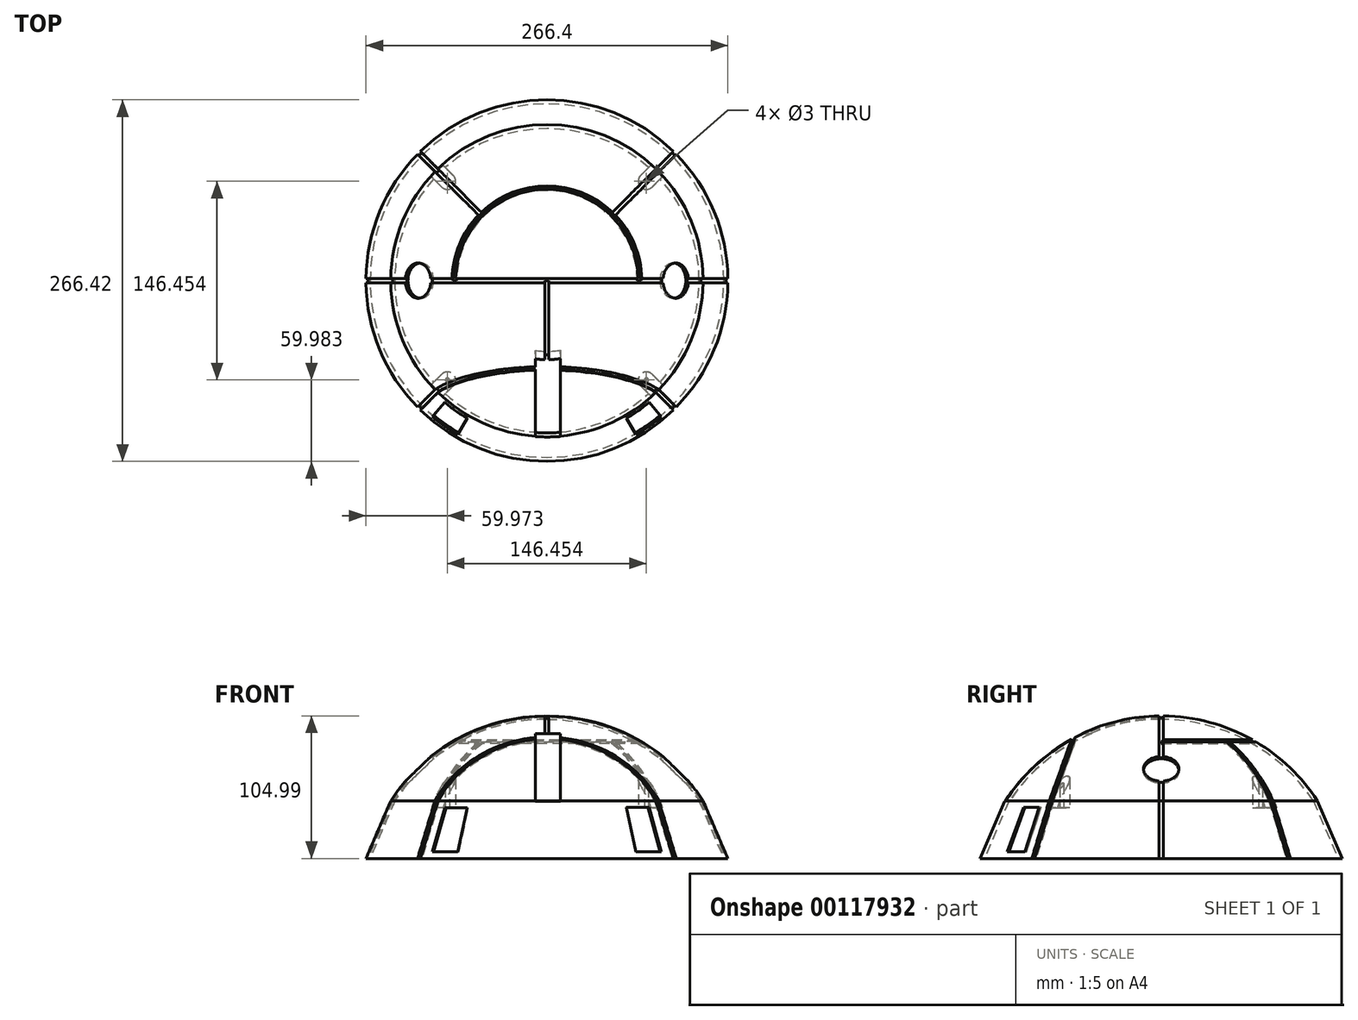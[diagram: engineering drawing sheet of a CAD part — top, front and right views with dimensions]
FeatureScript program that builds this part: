
annotation { "Feature Type Name" : "Feature", "Feature Type Description" : "" }
export const myFeature = defineFeature(function(context is Context, id is Id, definition is map)
    precondition{}
    {
        {
            var Q0;
            Q0=qCreatedBy(makeId("Front.planeOp"),FACE);
            var sketch = newSketch(context, id + "F0", { "sketchPlane" : qUnion([Q0])});
            skArc(sketch, "E0", {"start": v(114.97, 74.5) * mm, "mid": v(0, 137) * mm, "end": v(-114.97, 74.5) * mm});
            skLineSegment(sketch, "E1", {"start": v(-137, 0) * mm, "end": v(137, 0) * mm});
            skLineSegment(sketch, "E2", {"start": v(-133.21, 32) * mm, "end": v(133.21, 32) * mm});
            skLineSegment(sketch, "E3", {"start": v(-114.97, 74.5) * mm, "end": v(114.97, 74.5) * mm});
            skLineSegment(sketch, "E4", {"start": v(-114.97, 74.5) * mm, "end": v(-133.21, 32) * mm});
            skLineSegment(sketch, "E5", {"start": v(114.97, 74.5) * mm, "end": v(133.21, 32) * mm});
            skLineSegment(sketch, "E6", {"start": v(0, 137) * mm, "end": v(-99.44, 137) * mm, "construction": true});
            skLineSegment(sketch, "E7", {"start": v(0, 0) * mm, "end": v(0, 137) * mm});
            skArc(sketch, "E8", {"start": v(130.64, 32) * mm, "mid": v(0, 134.5) * mm, "end": v(-130.64, 32) * mm});
            skLineSegment(sketch, "E9", {"start": v(-111.98, 74.5) * mm, "end": v(-130.22, 32) * mm});
            skLineSegment(sketch, "E10", {"start": v(111.98, 74.5) * mm, "end": v(130.64, 32) * mm});
            skLineSegment(sketch, "E11", {"start": v(-111.98, 74.5) * mm, "end": v(-111.98, 32) * mm});
            skSolve(sketch);
        }
        {
            var Q0;
            {var subQ0=sQuery(id+"F0.wireOp",EDGE,"E4");Q0=makeQuery(id+"F0.imprint","IMPRINT",FACE,{"disambiguationData":[TD([[makeQuery(id+"F0.imprint","IMPRINT",EDGE,{"derivedFrom":subQ0}),1.0]])]});}
            var Q1;
            {var subQ0=sQuery(id+"F0.wireOp",EDGE,"E9");var subQ5=sQuery(id+"F0.wireOp",EDGE,"E2");var subQ7=makeQuery(id+"F0.imprint","INTERSECT",VERTEX,{"derivedFrom":[subQ5,subQ0]});Q1=makeQuery(id+"F0.imprint","IMPRINT",FACE,{"disambiguationData":[TD([[makeQuery(id+"F0.imprint","IMPRINT",EDGE,{"disambiguationData":[TD([[subQ7,1.0]])],"derivedFrom":subQ5}),1.0]])]});}
            var Q2;
            {var subQ0=sQuery(id+"F0.wireOp",EDGE,"y0KMc1JP-Vqzv-Jfck-pHGM-2HrRGkrfssAq");Q2=makeQuery(id+"F0.imprint","IMPRINT",FACE,{"disambiguationData":[TD([[makeQuery(id+"F0.imprint","IMPRINT",EDGE,{"derivedFrom":subQ0}),-1.0]])]});}
            var Q3;
            {var subQ1=sQuery(id+"F0.wireOp",EDGE,"E0");var subQ3=sQuery(id+"F0.wireOp",EDGE,"E7");var subQ4=makeQuery(id+"F0.imprint","INTERSECT",VERTEX,{"derivedFrom":[subQ1,subQ3]});Q3=makeQuery(id+"F0.imprint","IMPRINT",FACE,{"disambiguationData":[TD([[makeQuery(id+"F0.imprint","IMPRINT",EDGE,{"disambiguationData":[TD([[subQ4,1.0]])],"derivedFrom":subQ3}),1.0]])]});}
            var Q4;
            Q4=sQuery(id+"F0.wireOp",EDGE,"E7");
            revolve(context, id + "F1", {"entities" : qUnion([Q0, Q1, Q2, Q3]), "axis" : qUnion([Q4]), "revolveType" : RevolveType.FULL});
        }
        {
            var Q0;
            Q0=qCreatedBy(makeId("Top.planeOp"),FACE);
            cPlane(context, id + "F2", {"entities" : qUnion([Q0]), "cplaneType" : CPlaneType.OFFSET, "offset" : 74.5 * mm, "width" : 150 * mm, "height" : 150 * mm});
        }
        {
            var Q0;
            Q0=qCreatedBy(id+"F2.planeOp",FACE);
            var sketch = newSketch(context, id + "F3", { "sketchPlane" : qUnion([Q0])});
            skLineSegment(sketch, "E12", {"start": v(0, 0) * mm, "end": v(-58.68, 0) * mm, "construction": true});
            skLineSegment(sketch, "E13.bottom", {"start": v(-113.47, 1.5) * mm, "end": v(-116.47, 1.5) * mm});
            skLineSegment(sketch, "E13.top", {"start": v(-113.47, -1.5) * mm, "end": v(-116.47, -1.5) * mm});
            skLineSegment(sketch, "E13.left", {"start": v(-113.47, 1.5) * mm, "end": v(-113.47, -1.5) * mm});
            skLineSegment(sketch, "E13.right", {"start": v(-116.47, 1.5) * mm, "end": v(-116.47, -1.5) * mm});
            skPoint(sketch, "E13.middle", {"position": v(-114.97, 0) * mm});
            skLineSegment(sketch, "E14.1.0", {"start": v(-81.3, -79.18) * mm, "end": v(-83.42, -81.3) * mm});
            skLineSegment(sketch, "E14.1.1", {"start": v(-81.3, -79.18) * mm, "end": v(-79.18, -81.3) * mm});
            skLineSegment(sketch, "E14.1.2", {"start": v(-79.18, -81.3) * mm, "end": v(-81.3, -83.42) * mm});
            skLineSegment(sketch, "E14.1.3", {"start": v(-83.42, -81.3) * mm, "end": v(-81.3, -83.42) * mm});
            skLineSegment(sketch, "E14.2.0", {"start": v(-1.5, -113.47) * mm, "end": v(-1.5, -116.47) * mm});
            skLineSegment(sketch, "E14.2.1", {"start": v(-1.5, -113.47) * mm, "end": v(1.5, -113.47) * mm});
            skLineSegment(sketch, "E14.2.2", {"start": v(1.5, -113.47) * mm, "end": v(1.5, -116.47) * mm});
            skLineSegment(sketch, "E14.2.3", {"start": v(-1.5, -116.47) * mm, "end": v(1.5, -116.47) * mm});
            skLineSegment(sketch, "E14.3.0", {"start": v(79.18, -81.3) * mm, "end": v(81.3, -83.42) * mm});
            skLineSegment(sketch, "E14.3.1", {"start": v(79.18, -81.3) * mm, "end": v(81.3, -79.18) * mm});
            skLineSegment(sketch, "E14.3.2", {"start": v(81.3, -79.18) * mm, "end": v(83.42, -81.3) * mm});
            skLineSegment(sketch, "E14.3.3", {"start": v(81.3, -83.42) * mm, "end": v(83.42, -81.3) * mm});
            skLineSegment(sketch, "E14.4.0", {"start": v(113.47, -1.5) * mm, "end": v(116.47, -1.5) * mm});
            skLineSegment(sketch, "E14.4.1", {"start": v(113.47, -1.5) * mm, "end": v(113.47, 1.5) * mm});
            skLineSegment(sketch, "E14.4.2", {"start": v(113.47, 1.5) * mm, "end": v(116.47, 1.5) * mm});
            skLineSegment(sketch, "E14.4.3", {"start": v(116.47, -1.5) * mm, "end": v(116.47, 1.5) * mm});
            skLineSegment(sketch, "E14.5.0", {"start": v(81.3, 79.18) * mm, "end": v(83.42, 81.3) * mm});
            skLineSegment(sketch, "E14.5.1", {"start": v(81.3, 79.18) * mm, "end": v(79.18, 81.3) * mm});
            skLineSegment(sketch, "E14.5.2", {"start": v(79.18, 81.3) * mm, "end": v(81.3, 83.42) * mm});
            skLineSegment(sketch, "E14.5.3", {"start": v(83.42, 81.3) * mm, "end": v(81.3, 83.42) * mm});
            skLineSegment(sketch, "E14.6.0", {"start": v(1.5, 113.47) * mm, "end": v(1.5, 116.47) * mm});
            skLineSegment(sketch, "E14.6.1", {"start": v(1.5, 113.47) * mm, "end": v(-1.5, 113.47) * mm});
            skLineSegment(sketch, "E14.6.2", {"start": v(-1.5, 113.47) * mm, "end": v(-1.5, 116.47) * mm});
            skLineSegment(sketch, "E14.6.3", {"start": v(1.5, 116.47) * mm, "end": v(-1.5, 116.47) * mm});
            skLineSegment(sketch, "E14.7.0", {"start": v(-79.18, 81.3) * mm, "end": v(-81.3, 83.42) * mm});
            skLineSegment(sketch, "E14.7.1", {"start": v(-79.18, 81.3) * mm, "end": v(-81.3, 79.18) * mm});
            skLineSegment(sketch, "E14.7.2", {"start": v(-81.3, 79.18) * mm, "end": v(-83.42, 81.3) * mm});
            skLineSegment(sketch, "E14.7.3", {"start": v(-81.3, 83.42) * mm, "end": v(-83.42, 81.3) * mm});
            skPoint(sketch, "E14.center", {"position": v(0, 0) * mm});
            skLineSegment(sketch, "E15", {"start": v(81.3, -81.3) * mm, "end": v(-81.3, 81.3) * mm, "construction": true});
            skLineSegment(sketch, "E16", {"start": v(81.3, 81.3) * mm, "end": v(-81.3, -81.3) * mm, "construction": true});
            skLineSegment(sketch, "E17", {"start": v(-81.3, -81.3) * mm, "end": v(81.3, -81.3) * mm, "construction": true});
            skSolve(sketch);
        }
        {
            var Q0;
            Q0=makeQuery(id+"F3.imprint","IMPRINT",FACE,{"disambiguationData":[TD([[makeQuery(id+"F3.imprint","IMPRINT",EDGE,{"derivedFrom":sQuery(id+"F3.wireOp",EDGE,"E13.bottom")}),1.0]])]});
            var Q1;
            Q1=sQuery(id+"F0.wireOp",EDGE,"E4");
            sweep(context, id + "F4", {"operationType" : NewBodyOperationType.REMOVE, "profiles" : qUnion([Q0]), "path" : qUnion([Q1])});
        }
        {
            var Q0;
            Q0=makeQuery(id+"F3.imprint","IMPRINT",FACE,{"disambiguationData":[TD([[makeQuery(id+"F3.imprint","IMPRINT",EDGE,{"derivedFrom":sQuery(id+"F3.wireOp",EDGE,"E13.bottom")}),1.0]])]});
            var Q1;
            Q1=sQuery(id+"F0.wireOp",EDGE,"E0");
            sweep(context, id + "F5", {"operationType" : NewBodyOperationType.REMOVE, "profiles" : qUnion([Q0]), "path" : qUnion([Q1])});
        }
        {
            var Q0;
            Q0=makeQuery(id+"F3.imprint","IMPRINT",FACE,{"disambiguationData":[TD([[makeQuery(id+"F3.imprint","IMPRINT",EDGE,{"derivedFrom":sQuery(id+"F3.wireOp",EDGE,"E14.4.0")}),1.0]])]});
            var Q1;
            Q1=sQuery(id+"F0.wireOp",EDGE,"E5");
            sweep(context, id + "F6", {"operationType" : NewBodyOperationType.REMOVE, "profiles" : qUnion([Q0]), "path" : qUnion([Q1])});
        }
        {
            var Q0;
            Q0=qCreatedBy(makeId("Right.planeOp"),FACE);
            var sketch = newSketch(context, id + "F7", { "sketchPlane" : qUnion([Q0])});
            skArc(sketch, "E18", {"start": v(0, 137) * mm, "mid": v(-33.14, 132.93) * mm, "end": v(-64.32, 120.96) * mm});
            skLineSegment(sketch, "E19", {"start": v(0, 0) * mm, "end": v(-64.32, 120.96) * mm, "construction": true});
            skLineSegment(sketch, "E20", {"start": v(0, 137) * mm, "end": v(0, 0) * mm, "construction": true});
            skSolve(sketch);
        }
        {
            var Q0;
            Q0=qCreatedBy(makeId("Front.planeOp"),FACE);
            var sketch = newSketch(context, id + "F8", { "sketchPlane" : qUnion([Q0])});
            skLineSegment(sketch, "E21.bottom", {"start": v(1.5, 138.5) * mm, "end": v(-1.5, 138.5) * mm});
            skLineSegment(sketch, "E21.top", {"start": v(1.5, 135.5) * mm, "end": v(-1.5, 135.5) * mm});
            skLineSegment(sketch, "E21.left", {"start": v(1.5, 138.5) * mm, "end": v(1.5, 135.5) * mm});
            skLineSegment(sketch, "E21.right", {"start": v(-1.5, 138.5) * mm, "end": v(-1.5, 135.5) * mm});
            skPoint(sketch, "E21.middle", {"position": v(0, 137) * mm});
            skSolve(sketch);
        }
        {
            var Q0;
            Q0=makeQuery(id+"F8.imprint","IMPRINT",FACE,{"disambiguationData":[TD([[makeQuery(id+"F8.imprint","IMPRINT",EDGE,{"derivedFrom":sQuery(id+"F8.wireOp",EDGE,"E21.bottom")}),1.0]])]});
            var Q1;
            Q1=sQuery(id+"F7.wireOp",EDGE,"E18");
            sweep(context, id + "F9", {"operationType" : NewBodyOperationType.REMOVE, "profiles" : qUnion([Q0]), "path" : qUnion([Q1])});
        }
        {
            var Q0;
            Q0=qCreatedBy(makeId("Front.planeOp"),FACE);
            var sketch = newSketch(context, id + "F10", { "sketchPlane" : qUnion([Q0])});
            skCircle(sketch, "E22", {"center": v(0, 0) * mm, "radius": 137 * mm, "construction": true});
            skLineSegment(sketch, "E23", {"start": v(0, 0) * mm, "end": v(68.5, 118.65) * mm, "construction": true});
            skLineSegment(sketch, "E24", {"start": v(68.5, 118.65) * mm, "end": v(-68.5, 118.65) * mm});
            skLineSegment(sketch, "E25", {"start": v(-68.5, 118.65) * mm, "end": v(0, 0) * mm, "construction": true});
            skCircle(sketch, "E26", {"center": v(68.5, 118.65) * mm, "radius": 1.5 * mm});
            skLineSegment(sketch, "E27", {"start": v(67.75, 117.35) * mm, "end": v(69.05, 116.6) * mm});
            skLineSegment(sketch, "E28", {"start": v(69.05, 116.6) * mm, "end": v(70.55, 119.2) * mm});
            skLineSegment(sketch, "E29", {"start": v(67.75, 117.35) * mm, "end": v(66.45, 118.1) * mm});
            skLineSegment(sketch, "E30", {"start": v(70.55, 119.2) * mm, "end": v(67.95, 120.7) * mm});
            skLineSegment(sketch, "E31", {"start": v(67.95, 120.7) * mm, "end": v(66.45, 118.1) * mm});
            skLineSegment(sketch, "E32", {"start": v(0, 0) * mm, "end": v(104.95, 88.06) * mm, "construction": true});
            skLineSegment(sketch, "E33", {"start": v(0, 0) * mm, "end": v(-104.95, 88.06) * mm, "construction": true});
            skLineSegment(sketch, "E34", {"start": v(0, 0) * mm, "end": v(-114.71, 74.9) * mm, "construction": true});
            skLineSegment(sketch, "E35", {"start": v(-104.95, 88.06) * mm, "end": v(-81.98, 115.43) * mm});
            skLineSegment(sketch, "E36", {"start": v(104.95, 88.06) * mm, "end": v(89.01, 107.05) * mm});
            skSolve(sketch);
        }
        {
            var Q0;
            Q0=sQuery(id+"F10.wireOp",EDGE,"E24");
            cPlane(context, id + "F11", {"entities" : qUnion([Q0]), "cplaneType" : CPlaneType.LINE_ANGLE, "offset" : 25 * mm, "angle" : 90 * degree, "width" : 150 * mm, "height" : 150 * mm});
        }
        {
            var Q0;
            Q0=qCreatedBy(id+"F11.planeOp",FACE);
            var sketch = newSketch(context, id + "F12", { "sketchPlane" : qUnion([Q0])});
            skArc(sketch, "E37", {"start": v(68.5, 0) * mm, "mid": v(0, 68.5) * mm, "end": v(-68.5, 0) * mm});
            skLineSegment(sketch, "E38", {"start": v(-68.5, 0) * mm, "end": v(68.5, 0) * mm});
            skSolve(sketch);
        }
        {
            var Q0;
            {var subQ0=sQuery(id+"F10.wireOp",EDGE,"E26");var subQ3=makeQuery(id+"F10.imprint","INTERSECT",VERTEX,{"derivedFrom":[subQ0,sQuery(id+"F10.wireOp",EDGE,"E31")]});Q0=makeQuery(id+"F10.imprint","IMPRINT",FACE,{"disambiguationData":[TD([[makeQuery(id+"F10.imprint","IMPRINT",EDGE,{"disambiguationData":[TD([[subQ3,1.0]])],"derivedFrom":subQ0}),1.0]])]});}
            var Q1;
            {var subQ5=sQuery(id+"F10.wireOp",EDGE,"E29");Q1=makeQuery(id+"F10.imprint","IMPRINT",FACE,{"disambiguationData":[TD([[makeQuery(id+"F10.imprint","IMPRINT",EDGE,{"derivedFrom":subQ5}),-1.0]])]});}
            var Q2;
            {var subQ0=sQuery(id+"F10.wireOp",EDGE,"E31");var subQ1=sQuery(id+"F10.wireOp",EDGE,"E24");var subQ2=makeQuery(id+"F10.imprint","INTERSECT",VERTEX,{"derivedFrom":[subQ1,subQ0]});Q2=makeQuery(id+"F10.imprint","IMPRINT",FACE,{"disambiguationData":[TD([[makeQuery(id+"F10.imprint","IMPRINT",EDGE,{"disambiguationData":[TD([[subQ2,1.0]])],"derivedFrom":subQ1}),-1.0]])]});}
            var Q3;
            {var subQ0=sQuery(id+"F10.wireOp",EDGE,"E31");var subQ1=sQuery(id+"F10.wireOp",EDGE,"E26");var subQ2=makeQuery(id+"F10.imprint","INTERSECT",VERTEX,{"derivedFrom":[subQ1,subQ0]});Q3=makeQuery(id+"F10.imprint","IMPRINT",FACE,{"disambiguationData":[TD([[makeQuery(id+"F10.imprint","IMPRINT",EDGE,{"disambiguationData":[TD([[subQ2,1.0]])],"derivedFrom":subQ1}),-1.0]])]});}
            var Q4;
            {var subQ0=sQuery(id+"F10.wireOp",EDGE,"E30");var subQ1=sQuery(id+"F10.wireOp",EDGE,"E26");var subQ2=makeQuery(id+"F10.imprint","INTERSECT",VERTEX,{"derivedFrom":[subQ1,subQ0]});Q4=makeQuery(id+"F10.imprint","IMPRINT",FACE,{"disambiguationData":[TD([[makeQuery(id+"F10.imprint","IMPRINT",EDGE,{"disambiguationData":[TD([[subQ2,1.0]])],"derivedFrom":subQ1}),-1.0]])]});}
            var Q5;
            {var subQ0=sQuery(id+"F10.wireOp",EDGE,"E27");Q5=makeQuery(id+"F10.imprint","IMPRINT",FACE,{"disambiguationData":[TD([[makeQuery(id+"F10.imprint","IMPRINT",EDGE,{"derivedFrom":subQ0}),1.0]])]});}
            var Q6;
            Q6=sQuery(id+"F12.wireOp",EDGE,"E37");
            sweep(context, id + "F13", {"operationType" : NewBodyOperationType.REMOVE, "profiles" : qUnion([Q0, Q1, Q2, Q3, Q4, Q5]), "path" : qUnion([Q6])});
        }
        {
            var Q0;
            Q0=sQuery(id+"F3.wireOp",EDGE,"E16");
            cPlane(context, id + "F14", {"entities" : qUnion([Q0]), "cplaneType" : CPlaneType.LINE_ANGLE, "offset" : 25 * mm, "angle" : 90 * degree, "width" : 150 * mm, "height" : 150 * mm});
        }
        {
            var Q0;
            Q0=qCreatedBy(id+"F14.planeOp",FACE);
            var sketch = newSketch(context, id + "F15", { "sketchPlane" : qUnion([Q0])});
            skLineSegment(sketch, "E39", {"start": v(202.35, 74.5) * mm, "end": v(-236.58, 74.5) * mm, "construction": true});
            skLineSegment(sketch, "E40", {"start": v(177.5, 32) * mm, "end": v(-236.58, 32) * mm, "construction": true});
            skLineSegment(sketch, "E41", {"start": v(114.93, 74.5) * mm, "end": v(133.21, 32) * mm});
            skLineSegment(sketch, "E42", {"start": v(69.47, 117.89) * mm, "end": v(69.47, 32) * mm});
            skLineSegment(sketch, "E43", {"start": v(69.47, 32) * mm, "end": v(133.21, 32) * mm});
            skArc(sketch, "E44.trimOffspring", {"start": v(115.04, 74.26) * mm, "mid": v(94.8, 98.73) * mm, "end": v(69.47, 117.89) * mm});
            skSolve(sketch);
        }
        {
            var Q0;
            Q0=makeQuery(id+"F3.imprint","IMPRINT",FACE,{"disambiguationData":[TD([[makeQuery(id+"F3.imprint","IMPRINT",EDGE,{"derivedFrom":sQuery(id+"F3.wireOp",EDGE,"E14.5.0")}),1.0]])]});
            var Q1;
            Q1=sQuery(id+"F15.wireOp",EDGE,"E41");
            sweep(context, id + "F16", {"operationType" : NewBodyOperationType.REMOVE, "profiles" : qUnion([Q0]), "path" : qUnion([Q1])});
        }
        {
            var Q0;
            Q0=makeQuery(id+"F3.imprint","IMPRINT",FACE,{"disambiguationData":[TD([[makeQuery(id+"F3.imprint","IMPRINT",EDGE,{"derivedFrom":sQuery(id+"F3.wireOp",EDGE,"E14.5.0")}),1.0]])]});
            var Q1;
            Q1=sQuery(id+"F15.wireOp",EDGE,"E44.trimOffspring");
            sweep(context, id + "F17", {"operationType" : NewBodyOperationType.REMOVE, "profiles" : qUnion([Q0]), "path" : qUnion([Q1])});
        }
        {
            var Q0;
            Q0=sQuery(id+"F3.wireOp",EDGE,"E15");
            cPlane(context, id + "F18", {"entities" : qUnion([Q0]), "cplaneType" : CPlaneType.LINE_ANGLE, "offset" : 25 * mm, "angle" : 90 * degree, "width" : 150 * mm, "height" : 150 * mm});
        }
        {
            var Q0;
            Q0=qCreatedBy(id+"F18.planeOp",FACE);
            var sketch = newSketch(context, id + "F19", { "sketchPlane" : qUnion([Q0])});
            skArc(sketch, "E45", {"start": v(-114.97, 74.5) * mm, "mid": v(-125.9, 54.03) * mm, "end": v(-133.21, 32) * mm});
            skLineSegment(sketch, "E46", {"start": v(-154.96, 32) * mm, "end": v(196.04, 32) * mm, "construction": true});
            skLineSegment(sketch, "E47", {"start": v(-136.76, 74.5) * mm, "end": v(202.22, 74.5) * mm, "construction": true});
            skLineSegment(sketch, "E48", {"start": v(114.97, 74.5) * mm, "end": v(133.21, 32) * mm});
            skLineSegment(sketch, "E49", {"start": v(68.48, 118.66) * mm, "end": v(68.48, 32) * mm});
            skLineSegment(sketch, "E50", {"start": v(68.48, 32) * mm, "end": v(133.21, 32) * mm});
            skArc(sketch, "E51.trimOffspring", {"start": v(114.97, 74.5) * mm, "mid": v(94.35, 99.34) * mm, "end": v(68.48, 118.66) * mm});
            skSolve(sketch);
        }
        {
            var Q0;
            Q0=makeQuery(id+"F3.imprint","IMPRINT",FACE,{"disambiguationData":[TD([[makeQuery(id+"F3.imprint","IMPRINT",EDGE,{"derivedFrom":sQuery(id+"F3.wireOp",EDGE,"E14.7.0")}),1.0]])]});
            var Q1;
            Q1=sQuery(id+"F19.wireOp",EDGE,"E48");
            sweep(context, id + "F20", {"operationType" : NewBodyOperationType.REMOVE, "profiles" : qUnion([Q0]), "path" : qUnion([Q1])});
        }
        {
            var Q0;
            Q0=makeQuery(id+"F3.imprint","IMPRINT",FACE,{"disambiguationData":[TD([[makeQuery(id+"F3.imprint","IMPRINT",EDGE,{"derivedFrom":sQuery(id+"F3.wireOp",EDGE,"E14.7.0")}),1.0]])]});
            var Q1;
            Q1=sQuery(id+"F19.wireOp",EDGE,"E51.trimOffspring");
            sweep(context, id + "F21", {"operationType" : NewBodyOperationType.REMOVE, "profiles" : qUnion([Q0]), "path" : qUnion([Q1])});
        }
        {
            var Q0;
            Q0=sQuery(id+"F15.wireOp",EDGE,"E40");
            cPlane(context, id + "F22", {"entities" : qUnion([Q0]), "cplaneType" : CPlaneType.LINE_ANGLE, "offset" : 25 * mm, "angle" : 90 * degree, "width" : 150 * mm, "height" : 150 * mm});
        }
        {
            var Q0;
            Q0=qCreatedBy(id+"F22.planeOp",FACE);
            var sketch = newSketch(context, id + "F23", { "sketchPlane" : qUnion([Q0])});
            skArc(sketch, "E52", {"start": v(-133.21, 32) * mm, "mid": v(125.9, -54.03) * mm, "end": v(-114.97, 74.5) * mm});
            skLineSegment(sketch, "E53", {"start": v(-186.25, 32) * mm, "end": v(184.2, 32) * mm, "construction": true});
            skLineSegment(sketch, "E54", {"start": v(-158.48, 74.5) * mm, "end": v(175.2, 74.5) * mm, "construction": true});
            skLineSegment(sketch, "E55", {"start": v(-114.97, 74.5) * mm, "end": v(-133.21, 32) * mm});
            skSolve(sketch);
        }
        {
            var Q0;
            Q0=makeQuery(id+"F3.imprint","IMPRINT",FACE,{"disambiguationData":[TD([[makeQuery(id+"F3.imprint","IMPRINT",EDGE,{"derivedFrom":sQuery(id+"F3.wireOp",EDGE,"E14.1.0")}),1.0]])]});
            var Q1;
            Q1=sQuery(id+"F23.wireOp",EDGE,"E55");
            sweep(context, id + "F24", {"operationType" : NewBodyOperationType.REMOVE, "profiles" : qUnion([Q0]), "path" : qUnion([Q1])});
        }
        {
            var Q0;
            Q0=sQuery(id+"F19.wireOp",EDGE,"E46");
            cPlane(context, id + "F25", {"entities" : qUnion([Q0]), "cplaneType" : CPlaneType.LINE_ANGLE, "offset" : 25 * mm, "angle" : 90 * degree, "width" : 150 * mm, "height" : 150 * mm});
        }
        {
            var Q0;
            Q0=qCreatedBy(id+"F25.planeOp",FACE);
            var sketch = newSketch(context, id + "F26", { "sketchPlane" : qUnion([Q0])});
            skArc(sketch, "E56", {"start": v(-133.21, 32) * mm, "mid": v(125.9, -54.03) * mm, "end": v(-114.97, 74.5) * mm});
            skLineSegment(sketch, "E57", {"start": v(-151.8, 74.5) * mm, "end": v(39.62, 74.5) * mm, "construction": true});
            skLineSegment(sketch, "E58", {"start": v(-155.93, 32) * mm, "end": v(41.16, 32) * mm, "construction": true});
            skLineSegment(sketch, "E59", {"start": v(-114.97, 74.5) * mm, "end": v(-133.21, 32) * mm});
            skSolve(sketch);
        }
        {
            var Q0;
            Q0=makeQuery(id+"F3.imprint","IMPRINT",FACE,{"disambiguationData":[TD([[makeQuery(id+"F3.imprint","IMPRINT",EDGE,{"derivedFrom":sQuery(id+"F3.wireOp",EDGE,"E14.3.0")}),1.0]])]});
            var Q1;
            Q1=sQuery(id+"F26.wireOp",EDGE,"E59");
            sweep(context, id + "F27", {"operationType" : NewBodyOperationType.REMOVE, "profiles" : qUnion([Q0]), "path" : qUnion([Q1])});
        }
        {
            var Q0;
            Q0=sQuery(id+"F3.wireOp",EDGE,"E17");
            cPlane(context, id + "F28", {"entities" : qUnion([Q0]), "cplaneType" : CPlaneType.LINE_ANGLE, "offset" : 25 * mm, "angle" : 340 * degree, "width" : 150 * mm, "height" : 150 * mm});
        }
        {
            var Q0;
            Q0=qCreatedBy(id+"F28.planeOp",FACE);
            var sketch = newSketch(context, id + "F29", { "sketchPlane" : qUnion([Q0])});
            skArc(sketch, "E60", {"start": v(81.3, 42.2) * mm, "mid": v(0, 91.25) * mm, "end": v(-81.3, 42.2) * mm});
            skSolve(sketch);
        }
        {
            var Q0;
            Q0=makeQuery(id+"F3.imprint","IMPRINT",FACE,{"disambiguationData":[TD([[makeQuery(id+"F3.imprint","IMPRINT",EDGE,{"derivedFrom":sQuery(id+"F3.wireOp",EDGE,"E14.1.0")}),1.0]])]});
            var Q1;
            Q1=sQuery(id+"F29.wireOp",EDGE,"E60");
            sweep(context, id + "F30", {"operationType" : NewBodyOperationType.REMOVE, "profiles" : qUnion([Q0]), "path" : qUnion([Q1])});
        }
        {
            var Q0;
            Q0=qCreatedBy(makeId("Front.planeOp"),FACE);
            cPlane(context, id + "F31", {"entities" : qUnion([Q0]), "cplaneType" : CPlaneType.OFFSET, "offset" : 150 * mm, "width" : 150 * mm, "height" : 150 * mm});
        }
        {
            var Q0;
            Q0=qCreatedBy(id+"F31.planeOp",FACE);
            var sketch = newSketch(context, id + "F32", { "sketchPlane" : qUnion([Q0])});
            skLineSegment(sketch, "E61", {"start": v(0, 0) * mm, "end": v(0, 142.08) * mm, "construction": true});
            skLineSegment(sketch, "E62.bottom", {"start": v(-8.62, 124) * mm, "end": v(10, 124) * mm});
            skLineSegment(sketch, "E62.top", {"start": v(-8.62, 74) * mm, "end": v(10, 74) * mm});
            skLineSegment(sketch, "E62.left", {"start": v(-8.62, 124) * mm, "end": v(-8.62, 74) * mm});
            skLineSegment(sketch, "E62.right", {"start": v(10, 124) * mm, "end": v(10, 74) * mm});
            skSolve(sketch);
        }
        {
            var Q0;
            Q0=makeQuery(id+"F32.imprint","IMPRINT",FACE,{"disambiguationData":[TD([[makeQuery(id+"F32.imprint","IMPRINT",EDGE,{"derivedFrom":sQuery(id+"F32.wireOp",EDGE,"E62.bottom")}),-1.0]])]});
            extrude(context, id + "F33", {"entities" : qUnion([Q0]), "operationType" : NewBodyOperationType.REMOVE, "oppositeDirection" : true, "depth" : 123.02 * mm});
        }
        {
            var Q0;
            Q0=sQuery(id+"F10.wireOp",EDGE,"E35");
            cPlane(context, id + "F34", {"entities" : qUnion([Q0]), "cplaneType" : CPlaneType.LINE_ANGLE, "offset" : 25 * mm, "angle" : 0 * degree, "width" : 150 * mm, "height" : 150 * mm});
        }
        {
            var Q0;
            Q0=qCreatedBy(id+"F34.planeOp",FACE);
            var sketch = newSketch(context, id + "F35", { "sketchPlane" : qUnion([Q0])});
            skCircle(sketch, "E63", {"center": v(0, 14.13) * mm, "radius": 13 * mm});
            skCircle(sketch, "E64", {"center": v(0, 14.13) * mm, "radius": 21.5 * mm, "construction": true});
            skSolve(sketch);
        }
        {
            var Q0;
            Q0=makeQuery(id+"F35.imprint","IMPRINT",FACE,{"disambiguationData":[TD([[makeQuery(id+"F35.imprint","IMPRINT",EDGE,{"derivedFrom":sQuery(id+"F35.wireOp",EDGE,"E63")}),1.0]])]});
            extrude(context, id + "F36", {"entities" : qUnion([Q0]), "operationType" : NewBodyOperationType.REMOVE, "depth" : 25 * mm});
        }
        {
            var Q0;
            Q0=sQuery(id+"F10.wireOp",EDGE,"E36");
            cPlane(context, id + "F37", {"entities" : qUnion([Q0]), "cplaneType" : CPlaneType.LINE_ANGLE, "offset" : 25 * mm, "angle" : 0 * degree, "width" : 150 * mm, "height" : 150 * mm});
        }
        {
            var Q0;
            Q0=qCreatedBy(id+"F37.planeOp",FACE);
            var sketch = newSketch(context, id + "F38", { "sketchPlane" : qUnion([Q0])});
            skCircle(sketch, "E65", {"center": v(0, 14.13) * mm, "radius": 13 * mm});
            skCircle(sketch, "E66", {"center": v(0, 14.13) * mm, "radius": 21.5 * mm, "construction": true});
            skSolve(sketch);
        }
        {
            var Q0;
            Q0=makeQuery(id+"F38.imprint","IMPRINT",FACE,{"disambiguationData":[TD([[makeQuery(id+"F38.imprint","IMPRINT",EDGE,{"derivedFrom":sQuery(id+"F38.wireOp",EDGE,"E65")}),1.0]])]});
            extrude(context, id + "F39", {"entities" : qUnion([Q0]), "operationType" : NewBodyOperationType.REMOVE, "oppositeDirection" : true, "depth" : 25 * mm});
        }
        {
            var Q0;
            Q0=qCreatedBy(makeId("Top.planeOp"),FACE);
            cPlane(context, id + "F40", {"entities" : qUnion([Q0]), "cplaneType" : CPlaneType.OFFSET, "offset" : 32 * mm, "width" : 150 * mm, "height" : 150 * mm});
        }
        {
            var Q0;
            Q0=qCreatedBy(id+"F40.planeOp",FACE);
            var sketch = newSketch(context, id + "F41", { "sketchPlane" : qUnion([Q0])});
            skArc(sketch, "E67", {"start": v(-85.55, -101.95) * mm, "mid": v(-76.33, -109.02) * mm, "end": v(-66.54, -115.25) * mm});
            skLineSegment(sketch, "E68", {"start": v(0, 0) * mm, "end": v(-85.55, -101.95) * mm, "construction": true});
            skLineSegment(sketch, "E69", {"start": v(0, 0) * mm, "end": v(-66.54, -115.25) * mm, "construction": true});
            skLineSegment(sketch, "E70", {"start": v(0, 0) * mm, "end": v(85.55, -101.95) * mm, "construction": true});
            skLineSegment(sketch, "E71", {"start": v(0, 0) * mm, "end": v(66.54, -115.25) * mm, "construction": true});
            skArc(sketch, "E72.trimOffspring", {"start": v(66.54, -115.25) * mm, "mid": v(76.33, -109.02) * mm, "end": v(85.55, -101.95) * mm});
            skSolve(sketch);
        }
        {
            var Q0;
            Q0=sQuery(id+"F41.wireOp",EDGE,"E68");
            cPlane(context, id + "F42", {"entities" : qUnion([Q0]), "cplaneType" : CPlaneType.LINE_ANGLE, "offset" : 25 * mm, "angle" : 90 * degree, "width" : 150 * mm, "height" : 150 * mm});
        }
        {
            var Q0;
            Q0=qCreatedBy(id+"F42.planeOp",FACE);
            var sketch = newSketch(context, id + "F43", { "sketchPlane" : qUnion([Q0])});
            skLineSegment(sketch, "E73", {"start": v(-155.46, 32) * mm, "end": v(-59.64, 32) * mm, "construction": true});
            skLineSegment(sketch, "E74", {"start": v(-156.19, 74.5) * mm, "end": v(-59.64, 74.5) * mm, "construction": true});
            skLineSegment(sketch, "E75", {"start": v(-114.74, 74.5) * mm, "end": v(-133.34, 32) * mm, "construction": true});
            skLineSegment(sketch, "E76", {"start": v(-138.35, 69.5) * mm, "end": v(-98.78, 69.5) * mm, "construction": true});
            skLineSegment(sketch, "E77", {"start": v(-139.73, 37) * mm, "end": v(-103.81, 37) * mm, "construction": true});
            skLineSegment(sketch, "E78", {"start": v(-118.57, 69.5) * mm, "end": v(-132.8, 37) * mm});
            skLineSegment(sketch, "E79", {"start": v(-129.52, 37) * mm, "end": v(-115.3, 69.5) * mm});
            skLineSegment(sketch, "E80", {"start": v(-118.57, 69.5) * mm, "end": v(-115.3, 69.5) * mm});
            skLineSegment(sketch, "E81", {"start": v(-132.8, 37) * mm, "end": v(-129.52, 37) * mm});
            skSolve(sketch);
        }
        {
            var Q0;
            Q0=makeQuery(id+"F43.imprint","IMPRINT",FACE,{"disambiguationData":[TD([[makeQuery(id+"F43.imprint","IMPRINT",EDGE,{"derivedFrom":sQuery(id+"F43.wireOp",EDGE,"E78")}),1.0]])]});
            var Q1;
            Q1=sQuery(id+"F41.wireOp",EDGE,"E67");
            sweep(context, id + "F44", {"operationType" : NewBodyOperationType.REMOVE, "profiles" : qUnion([Q0]), "path" : qUnion([Q1])});
        }
        {
            var Q0;
            Q0=sQuery(id+"F41.wireOp",EDGE,"E70");
            cPlane(context, id + "F45", {"entities" : qUnion([Q0]), "cplaneType" : CPlaneType.LINE_ANGLE, "offset" : 25 * mm, "angle" : 90 * degree, "width" : 150 * mm, "height" : 150 * mm});
        }
        {
            var Q0;
            Q0=qCreatedBy(id+"F45.planeOp",FACE);
            var sketch = newSketch(context, id + "F46", { "sketchPlane" : qUnion([Q0])});
            skLineSegment(sketch, "E82", {"start": v(-133.33, 32.01) * mm, "end": v(-115.18, 74.7) * mm, "construction": true});
            skLineSegment(sketch, "E83", {"start": v(-135.3, 74.51) * mm, "end": v(-97, 74.51) * mm});
            skLineSegment(sketch, "E84", {"start": v(-135.3, 69.51) * mm, "end": v(-92.23, 69.51) * mm});
            skLineSegment(sketch, "E85", {"start": v(-140.39, 32.01) * mm, "end": v(-102.15, 32.01) * mm});
            skLineSegment(sketch, "E86", {"start": v(-140.08, 37.01) * mm, "end": v(-97.77, 37.01) * mm});
            skLineSegment(sketch, "E87", {"start": v(-119.01, 69.51) * mm, "end": v(-132.83, 37.01) * mm});
            skLineSegment(sketch, "E88", {"start": v(-115.75, 69.51) * mm, "end": v(-129.57, 37.01) * mm});
            skLineSegment(sketch, "E89", {"start": v(-129.57, 37.01) * mm, "end": v(-132.83, 37.01) * mm});
            skLineSegment(sketch, "E90", {"start": v(-115.75, 69.51) * mm, "end": v(-119.01, 69.51) * mm});
            skSolve(sketch);
        }
        {
            var Q0;
            Q0=makeQuery(id+"F46.imprint","IMPRINT",FACE,{"disambiguationData":[TD([[makeQuery(id+"F46.imprint","IMPRINT",EDGE,{"derivedFrom":sQuery(id+"F46.wireOp",EDGE,"E87")}),1.0]])]});
            var Q1;
            Q1=sQuery(id+"F41.wireOp",EDGE,"E72.trimOffspring");
            sweep(context, id + "F47", {"operationType" : NewBodyOperationType.REMOVE, "profiles" : qUnion([Q0]), "path" : qUnion([Q1])});
        }
        {
            var Q0;
            Q0=qCreatedBy(id+"F2.planeOp",FACE);
            cPlane(context, id + "F48", {"entities" : qUnion([Q0]), "cplaneType" : CPlaneType.OFFSET, "offset" : 5 * mm, "oppositeDirection" : true, "width" : 150 * mm, "height" : 150 * mm});
        }
        {
            var Q0;
            Q0=qCreatedBy(id+"F48.planeOp",FACE);
            var sketch = newSketch(context, id + "F49", { "sketchPlane" : qUnion([Q0])});
            skArc(sketch, "E91", {"start": v(-85.45, -76.96) * mm, "mid": v(-81.32, -81.32) * mm, "end": v(-76.96, -85.45) * mm});
            skLineSegment(sketch, "E92", {"start": v(0, 0) * mm, "end": v(-115, 0) * mm, "construction": true});
            skLineSegment(sketch, "E93", {"start": v(-115, 0) * mm, "end": v(0, 0) * mm, "construction": true});
            skLineSegment(sketch, "E94", {"start": v(0, 0) * mm, "end": v(-81.32, -81.32) * mm, "construction": true});
            skCircle(sketch, "E95", {"center": v(-73.23, -73.23) * mm, "radius": 6 * mm});
            skCircle(sketch, "E96", {"center": v(-73.23, -73.23) * mm, "radius": 1.5 * mm});
            skLineSegment(sketch, "E97", {"start": v(-73.23, -73.23) * mm, "end": v(-66.8, -79.65) * mm, "construction": true});
            skLineSegment(sketch, "E98", {"start": v(-66.8, -79.65) * mm, "end": v(-78.95, -67.5) * mm, "construction": true});
            skLineSegment(sketch, "E99", {"start": v(-68.98, -77.47) * mm, "end": v(-76.96, -85.45) * mm});
            skLineSegment(sketch, "E100", {"start": v(-77.47, -68.98) * mm, "end": v(-85.45, -76.96) * mm});
            skLineSegment(sketch, "E101.1.0", {"start": v(77.47, -68.98) * mm, "end": v(85.45, -76.96) * mm});
            skArc(sketch, "E101.1.1", {"start": v(76.96, -85.45) * mm, "mid": v(81.32, -81.32) * mm, "end": v(85.45, -76.96) * mm});
            skLineSegment(sketch, "E101.1.2", {"start": v(68.98, -77.47) * mm, "end": v(76.96, -85.45) * mm});
            skCircle(sketch, "E101.1.3", {"center": v(73.23, -73.23) * mm, "radius": 6 * mm});
            skCircle(sketch, "E101.1.4", {"center": v(73.23, -73.23) * mm, "radius": 1.5 * mm});
            skLineSegment(sketch, "E101.2.0", {"start": v(68.98, 77.47) * mm, "end": v(76.96, 85.45) * mm});
            skArc(sketch, "E101.2.1", {"start": v(85.45, 76.96) * mm, "mid": v(81.32, 81.32) * mm, "end": v(76.96, 85.45) * mm});
            skLineSegment(sketch, "E101.2.2", {"start": v(77.47, 68.98) * mm, "end": v(85.45, 76.96) * mm});
            skCircle(sketch, "E101.2.3", {"center": v(73.23, 73.23) * mm, "radius": 6 * mm});
            skCircle(sketch, "E101.2.4", {"center": v(73.23, 73.23) * mm, "radius": 1.5 * mm});
            skLineSegment(sketch, "E101.3.0", {"start": v(-77.47, 68.98) * mm, "end": v(-85.45, 76.96) * mm});
            skArc(sketch, "E101.3.1", {"start": v(-76.96, 85.45) * mm, "mid": v(-81.32, 81.32) * mm, "end": v(-85.45, 76.96) * mm});
            skLineSegment(sketch, "E101.3.2", {"start": v(-68.98, 77.47) * mm, "end": v(-76.96, 85.45) * mm});
            skCircle(sketch, "E101.3.3", {"center": v(-73.23, 73.23) * mm, "radius": 6 * mm});
            skCircle(sketch, "E101.3.4", {"center": v(-73.23, 73.23) * mm, "radius": 1.5 * mm});
            skSolve(sketch);
        }
        {
            var Q0;
            Q0=makeQuery(id+"F49.imprint","IMPRINT",FACE,{"disambiguationData":[TD([[makeQuery(id+"F49.imprint","IMPRINT",EDGE,{"derivedFrom":sQuery(id+"F49.wireOp",EDGE,"E91")}),1.0]])]});
            var Q1;
            Q1=makeQuery(id+"F49.imprint","IMPRINT",FACE,{"disambiguationData":[TD([[makeQuery(id+"F49.imprint","IMPRINT",EDGE,{"derivedFrom":sQuery(id+"F49.wireOp",EDGE,"E96")}),-1.0]])]});
            var Q2;
            {var subQ0=sQuery(id+"F49.wireOp",EDGE,"E101.3.0");Q2=makeQuery(id+"F49.imprint","IMPRINT",FACE,{"disambiguationData":[TD([[makeQuery(id+"F49.imprint","IMPRINT",EDGE,{"derivedFrom":subQ0}),-1.0]])]});}
            var Q3;
            Q3=makeQuery(id+"F49.imprint","IMPRINT",FACE,{"disambiguationData":[TD([[makeQuery(id+"F49.imprint","IMPRINT",EDGE,{"derivedFrom":sQuery(id+"F49.wireOp",EDGE,"E101.3.4")}),-1.0]])]});
            var Q4;
            {var subQ0=sQuery(id+"F49.wireOp",EDGE,"E101.2.0");Q4=makeQuery(id+"F49.imprint","IMPRINT",FACE,{"disambiguationData":[TD([[makeQuery(id+"F49.imprint","IMPRINT",EDGE,{"derivedFrom":subQ0}),-1.0]])]});}
            var Q5;
            Q5=makeQuery(id+"F49.imprint","IMPRINT",FACE,{"disambiguationData":[TD([[makeQuery(id+"F49.imprint","IMPRINT",EDGE,{"derivedFrom":sQuery(id+"F49.wireOp",EDGE,"E101.2.4")}),-1.0]])]});
            var Q6;
            {var subQ0=sQuery(id+"F49.wireOp",EDGE,"E101.1.0");Q6=makeQuery(id+"F49.imprint","IMPRINT",FACE,{"disambiguationData":[TD([[makeQuery(id+"F49.imprint","IMPRINT",EDGE,{"derivedFrom":subQ0}),-1.0]])]});}
            var Q7;
            Q7=makeQuery(id+"F49.imprint","IMPRINT",FACE,{"disambiguationData":[TD([[makeQuery(id+"F49.imprint","IMPRINT",EDGE,{"derivedFrom":sQuery(id+"F49.wireOp",EDGE,"E101.1.4")}),-1.0]])]});
            var Q8;
            Q8=makeQuery(id+"F1.opRevolve","SWEPT_BODY",BODY,{"disambiguationData":[OSD([sQuery(id+"F0.wireOp",EDGE,"E0"),sQuery(id+"F0.wireOp",EDGE,"E2"),sQuery(id+"F0.wireOp",EDGE,"E4"),sQuery(id+"F0.wireOp",EDGE,"E7"),sQuery(id+"F0.wireOp",EDGE,"E8"),sQuery(id+"F0.wireOp",EDGE,"E9")])]});
            extrude(context, id + "F50", {"entities" : qUnion([Q0, Q1, Q2, Q3, Q4, Q5, Q6, Q7]), "operationType" : NewBodyOperationType.ADD, "endBound" : BoundingType.UP_TO_BODY, "endBoundEntityBody" : qUnion([Q8]), "depth" : 25 * mm});
        }
    });
